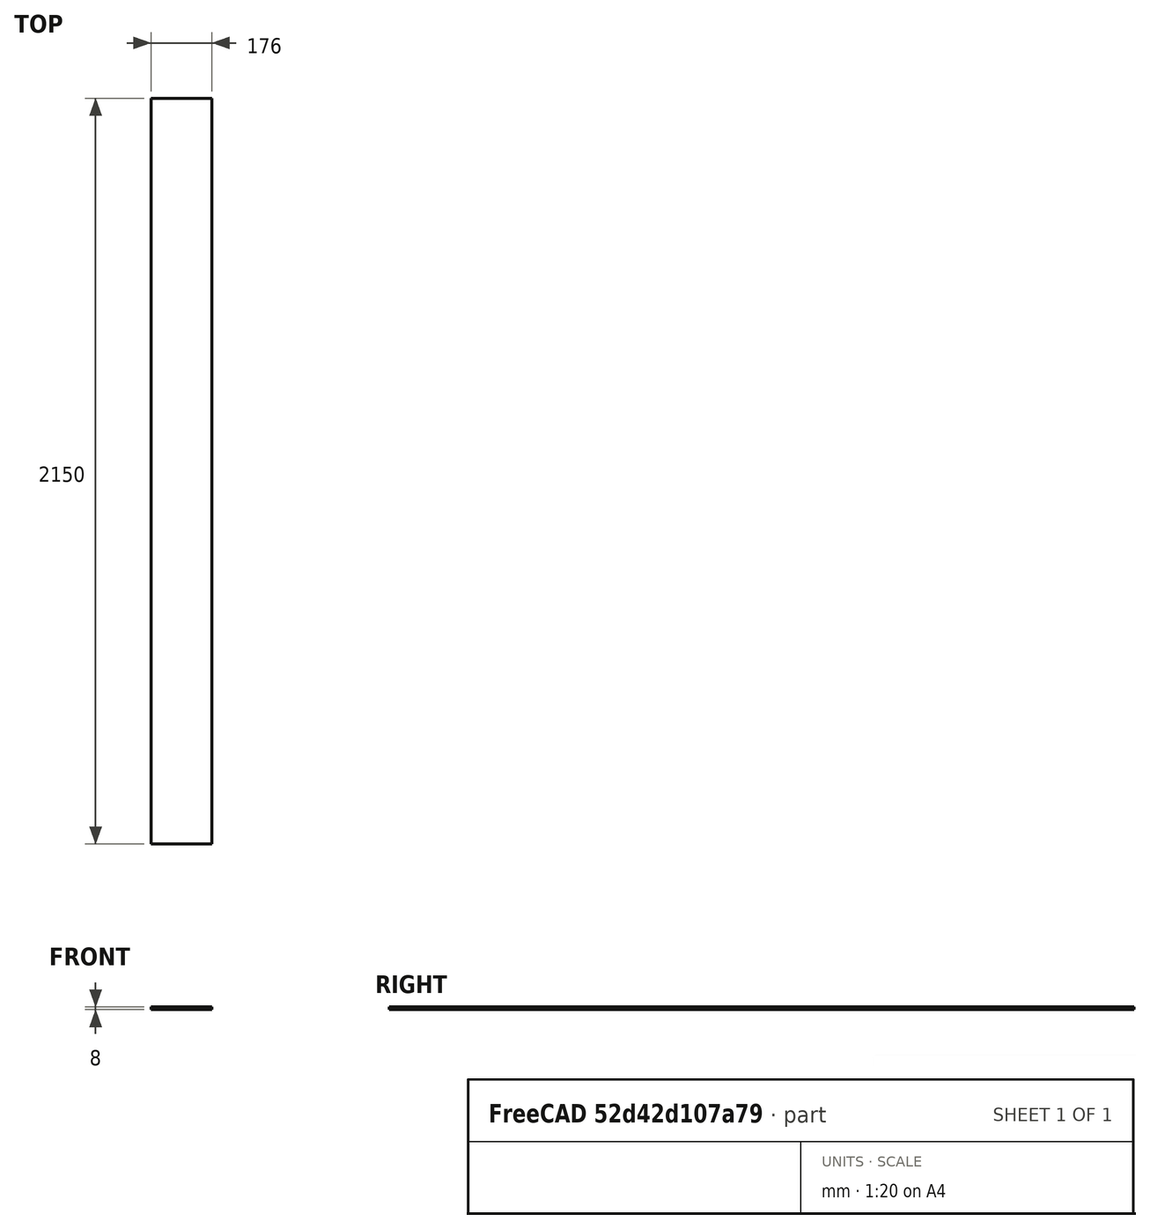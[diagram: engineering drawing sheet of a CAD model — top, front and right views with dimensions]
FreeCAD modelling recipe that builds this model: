
FCSTD DOCUMENT  (FreeCAD 0.15R4671 (Git))
Label: Vitre_old
License: All rights reserved
LicenseURL: http://en.wikipedia.org/wiki/All_rights_reserved
objects: Sketcher::SketchObject×1, PartDesign::Pad×1
note: 3 computed .brp shape members not serialized (recipe doc carries the construction recipe); baked Part::Feature solids carry a one-line shape summary decoded from their .brp

FEATURE [Sketcher::SketchObject] Sketch
  Placement = pos=(0,0,0) rot=(1,0,0;1.5708rad)
  sketch-geometry (4):
    g0: LineSegment StartX=-88 StartY=4 StartZ=0 EndX=88 EndY=4 EndZ=0
    g1: LineSegment StartX=88 StartY=4 StartZ=0 EndX=88 EndY=-4 EndZ=0
    g2: LineSegment StartX=88 StartY=-4 StartZ=0 EndX=-88 EndY=-4 EndZ=0
    g3: LineSegment StartX=-88 StartY=-4 StartZ=0 EndX=-88 EndY=4 EndZ=0
  constraints (12):
    c: Coincident(g0,g1)
    c: Coincident(g1,g2)
    c: Coincident(g2,g3)
    c: Coincident(g3,g0)
    c: Horizontal(g0)
    c: Horizontal(g2)
    c: Vertical(g1)
    c: Vertical(g3)
    c: DistanceX(g0,g0) = 176
    c: DistanceY(g0,g2) = -8
    c: Symmetric(g0,g0,g-2)
    c: Symmetric(g0,g2,g-1)
FEATURE [PartDesign::Pad] Pad
  Length = 2150
  Length2 = 100
  Midplane = true
  Placement = pos=(0,0,0) rot=(1,0,0;1.5708rad)
  Sketch = -> Sketch
  Type = 0
